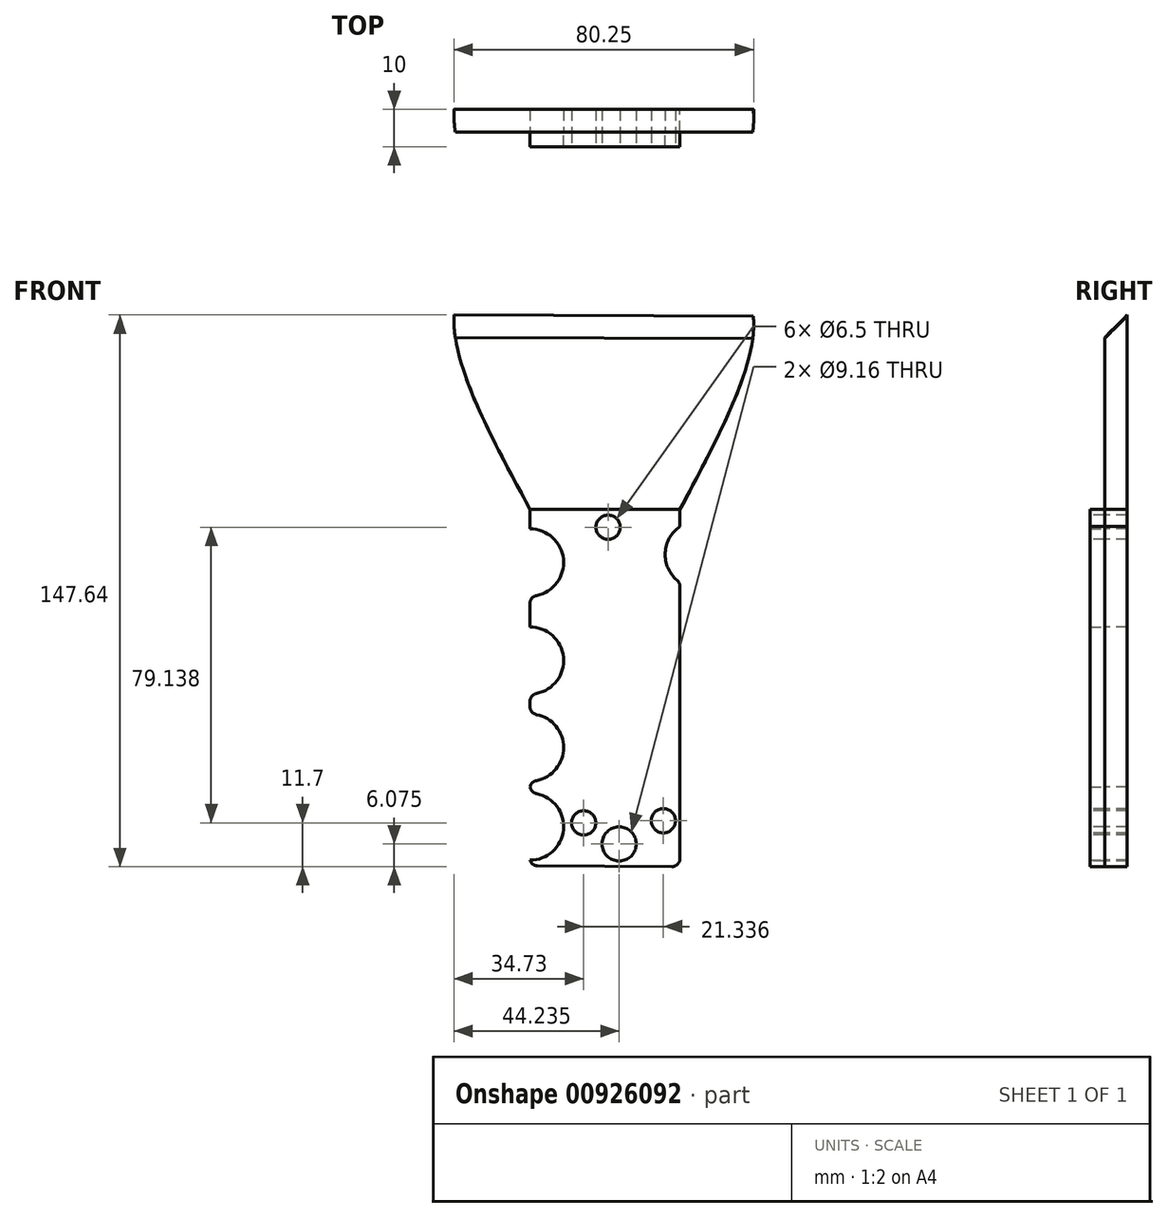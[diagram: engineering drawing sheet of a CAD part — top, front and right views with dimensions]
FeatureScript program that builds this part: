
annotation { "Feature Type Name" : "Feature", "Feature Type Description" : "" }
export const myFeature = defineFeature(function(context is Context, id is Id, definition is map)
    precondition{}
    {
        {
            var Q0;
            Q0=qCreatedBy(makeId("Front.planeOp"),FACE);
            var sketch = newSketch(context, id + "F0", { "sketchPlane" : qUnion([Q0])});
            skLineSegment(sketch, "E0.bottom", {"start": v(-40.83, 99.08) * mm, "end": v(39.17, 99.08) * mm});
            skLineSegment(sketch, "E0.top", {"start": v(-40.83, -50.92) * mm, "end": v(39.17, -50.92) * mm});
            skLineSegment(sketch, "E0.left", {"start": v(-40.83, 99.08) * mm, "end": v(-40.83, -50.92) * mm});
            skLineSegment(sketch, "E0.right", {"start": v(39.17, 99.08) * mm, "end": v(39.17, -50.92) * mm});
            skSolve(sketch);
        }
        {
            var Q0;
            Q0=makeQuery(id+"F0.imprint","IMPRINT",FACE,{"disambiguationData":[TD([[makeQuery(id+"F0.imprint","IMPRINT",EDGE,{"derivedFrom":sQuery(id+"F0.wireOp",EDGE,"E0.bottom")}),-1.0]])]});
            var sketch = newSketch(context, id + "F1", { "sketchPlane" : qUnion([Q0])});
            skLineSegment(sketch, "E1", {"start": v(-41.28, 46.44) * mm, "end": v(36.17, 46.44) * mm});
            skLineSegment(sketch, "E2", {"start": v(36.17, 46.44) * mm, "end": v(-20.92, 46.44) * mm});
            skLineSegment(sketch, "E3", {"start": v(-20.92, 46.44) * mm, "end": v(-20.92, -48.99) * mm});
            skLineSegment(sketch, "E4", {"start": v(19.24, 46.44) * mm, "end": v(19.24, -49.2) * mm});
            skLineSegment(sketch, "E5", {"start": v(-20.92, -48.99) * mm, "end": v(19.24, -49.2) * mm});
            skFitSpline(sketch, "E6", {"points": [v(-20.92, 46.44) * mm, v(-41.1, 99.43) * mm, v(-28.22, 117.54) * mm], "startDerivative": vector(-53.21, 98.2) * mm, "endDerivative": vector(46.25, 39.49) * mm});
            skFitSpline(sketch, "E7", {"points": [v(19.24, 46.44) * mm, v(38.71, 99.16) * mm, v(24.45, 116.44) * mm], "startDerivative": vector(52.8, 98.69) * mm, "endDerivative": vector(-50.13, 36.65) * mm});
            skLineSegment(sketch, "E8", {"start": v(-41.1, 99.43) * mm, "end": v(38.71, 99.16) * mm});
            skSolve(sketch);
        }
        {
            var Q0;
            Q0 = qSketchRegion(id + "F1", true);
            extrude(context, id + "F2", {"entities" : qUnion([Q0]), "depth" : 6 * mm, "offsetDistance" : 25 * mm});
        }
        {
            var Q0;
            Q0=makeQuery(id+"F2.opExtrude","CAP_EDGE",EDGE,{"disambiguationData":[OSD([sQuery(id+"F1.wireOp",EDGE,"E8")])],"isStart":false});
            chamfer(context, id + "F3", {"entities" : qUnion([Q0]), "width" : 7 * mm, "tangentPropagation" : true});
        }
        {
            var Q0;
            Q0=makeQuery(id+"F2.opExtrude","CAP_FACE",FACE,{"disambiguationData":[OSD([sQuery(id+"F1.wireOp",EDGE,"E3"),sQuery(id+"F1.wireOp",EDGE,"E4"),sQuery(id+"F1.wireOp",EDGE,"E5"),sQuery(id+"F1.wireOp",EDGE,"E6"),sQuery(id+"F1.wireOp",EDGE,"E7"),sQuery(id+"F1.wireOp",EDGE,"E8")])],"isStart":false});
            var sketch = newSketch(context, id + "F4", { "sketchPlane" : qUnion([Q0])});
            skCircle(sketch, "E9", {"center": v(-20.92, 32.19) * mm, "radius": 9 * mm});
            skCircle(sketch, "E10", {"center": v(-20.92, 5.95) * mm, "radius": 9 * mm});
            skCircle(sketch, "E11", {"center": v(-20.92, -17.34) * mm, "radius": 9 * mm});
            skCircle(sketch, "E12", {"center": v(-20.92, -38.48) * mm, "radius": 9 * mm});
            skSolve(sketch);
        }
        {
            var Q0;
            {var subQ9=sQuery(id+"F1.wireOp",EDGE,"E4");Q0=makeQuery(id+"F4.imprint","IMPRINT",FACE,{"disambiguationData":[TD([[makeQuery(id+"F4.imprint","IMPRINT",EDGE,{"derivedFrom":makeQuery(id+"F2.opExtrude","CAP_EDGE",EDGE,{"disambiguationData":[OSD([subQ9])],"isStart":false})}),-1.0]])]});}
            var sketch = newSketch(context, id + "F5", { "sketchPlane" : qUnion([Q0])});
            skCircle(sketch, "E13", {"center": v(24.28, 34.33) * mm, "radius": 9 * mm});
            skSolve(sketch);
        }
        {
            var Q0;
            {var subQ0=sQuery(id+"F4.wireOp",EDGE,"E9");var subQ1=makeQuery(id+"F2.opExtrude","CAP_EDGE",EDGE,{"disambiguationData":[OSD([sQuery(id+"F1.wireOp",EDGE,"E3")])],"isStart":false});var subQ2=makeQuery(id+"F4.imprint","INTERSECT",VERTEX,{"disambiguationData":[OD(0.0)],"derivedFrom":[subQ1,subQ0]});Q0=makeQuery(id+"F4.imprint","IMPRINT",FACE,{"disambiguationData":[TD([[makeQuery(id+"F4.imprint","IMPRINT",EDGE,{"disambiguationData":[TD([[subQ2,1.0]])],"derivedFrom":subQ0}),1.0]])]});}
            var Q1;
            {var subQ0=sQuery(id+"F4.wireOp",EDGE,"E10");var subQ1=makeQuery(id+"F2.opExtrude","CAP_EDGE",EDGE,{"disambiguationData":[OSD([sQuery(id+"F1.wireOp",EDGE,"E3")])],"isStart":false});var subQ2=makeQuery(id+"F4.imprint","INTERSECT",VERTEX,{"disambiguationData":[OD(0.0)],"derivedFrom":[subQ1,subQ0]});Q1=makeQuery(id+"F4.imprint","IMPRINT",FACE,{"disambiguationData":[TD([[makeQuery(id+"F4.imprint","IMPRINT",EDGE,{"disambiguationData":[TD([[subQ2,1.0]])],"derivedFrom":subQ0}),1.0]])]});}
            var Q2;
            {var subQ0=sQuery(id+"F4.wireOp",EDGE,"E11");var subQ1=makeQuery(id+"F2.opExtrude","CAP_EDGE",EDGE,{"disambiguationData":[OSD([sQuery(id+"F1.wireOp",EDGE,"E3")])],"isStart":false});var subQ2=makeQuery(id+"F4.imprint","INTERSECT",VERTEX,{"disambiguationData":[OD(0.0)],"derivedFrom":[subQ1,subQ0]});Q2=makeQuery(id+"F4.imprint","IMPRINT",FACE,{"disambiguationData":[TD([[makeQuery(id+"F4.imprint","IMPRINT",EDGE,{"disambiguationData":[TD([[subQ2,-1.0]])],"derivedFrom":subQ0}),1.0]])]});}
            var Q3;
            {var subQ0=sQuery(id+"F4.wireOp",EDGE,"E12");var subQ1=makeQuery(id+"F2.opExtrude","CAP_EDGE",EDGE,{"disambiguationData":[OSD([sQuery(id+"F1.wireOp",EDGE,"E3")])],"isStart":false});var subQ2=makeQuery(id+"F4.imprint","INTERSECT",VERTEX,{"disambiguationData":[OD(0.0)],"derivedFrom":[subQ1,subQ0]});Q3=makeQuery(id+"F4.imprint","IMPRINT",FACE,{"disambiguationData":[TD([[makeQuery(id+"F4.imprint","IMPRINT",EDGE,{"disambiguationData":[TD([[subQ2,-1.0]])],"derivedFrom":subQ0}),1.0]])]});}
            var Q4;
            {var subQ0=sQuery(id+"F5.wireOp",EDGE,"E13");var subQ1=makeQuery(id+"F4.imprint","IMPRINT",EDGE,{"derivedFrom":makeQuery(id+"F2.opExtrude","CAP_EDGE",EDGE,{"disambiguationData":[OSD([sQuery(id+"F1.wireOp",EDGE,"E4")])],"isStart":false})});var subQ2=makeQuery(id+"F5.imprint","INTERSECT",VERTEX,{"disambiguationData":[OD(0.0)],"derivedFrom":[subQ1,subQ0]});Q4=makeQuery(id+"F5.imprint","IMPRINT",FACE,{"disambiguationData":[TD([[makeQuery(id+"F5.imprint","IMPRINT",EDGE,{"disambiguationData":[TD([[subQ2,-1.0]])],"derivedFrom":subQ0}),1.0]])]});}
            extrude(context, id + "F6", {"entities" : qUnion([Q0, Q1, Q2, Q3, Q4]), "operationType" : NewBodyOperationType.REMOVE, "oppositeDirection" : true, "depth" : 25 * mm, "offsetDistance" : 25 * mm});
        }
        {
            var Q0;
            {var subQ0=sQuery(id+"F4.wireOp",EDGE,"E9");var subQ1=sQuery(id+"F1.wireOp",EDGE,"E3");Q0=makeQuery(id+"F6.boolean.opBoolean","COPY",EDGE,{"derivedFrom":makeQuery(id+"F6.opExtrude","SWEPT_EDGE",EDGE,{"disambiguationData":[OSD([subQ1,subQ0]),TDD([makeQuery(id+"F4.imprint","INTERSECT",VERTEX,{"disambiguationData":[OD(1.0)],"derivedFrom":[makeQuery(id+"F2.opExtrude","CAP_EDGE",EDGE,{"disambiguationData":[OSD([subQ1])],"isStart":false}),subQ0]})])]})});}
            var Q1;
            {var subQ0=sQuery(id+"F4.wireOp",EDGE,"E10");var subQ1=sQuery(id+"F1.wireOp",EDGE,"E3");Q1=makeQuery(id+"F6.boolean.opBoolean","COPY",EDGE,{"derivedFrom":makeQuery(id+"F6.opExtrude","SWEPT_EDGE",EDGE,{"disambiguationData":[OSD([subQ1,subQ0]),TDD([makeQuery(id+"F4.imprint","INTERSECT",VERTEX,{"disambiguationData":[OD(1.0)],"derivedFrom":[makeQuery(id+"F2.opExtrude","CAP_EDGE",EDGE,{"disambiguationData":[OSD([subQ1])],"isStart":false}),subQ0]})])]})});}
            var Q2;
            {var subQ0=sQuery(id+"F4.wireOp",EDGE,"E11");var subQ1=sQuery(id+"F1.wireOp",EDGE,"E3");Q2=makeQuery(id+"F6.boolean.opBoolean","COPY",EDGE,{"derivedFrom":makeQuery(id+"F6.opExtrude","SWEPT_EDGE",EDGE,{"disambiguationData":[OSD([subQ1,subQ0]),TDD([makeQuery(id+"F4.imprint","INTERSECT",VERTEX,{"disambiguationData":[OD(1.0)],"derivedFrom":[makeQuery(id+"F2.opExtrude","CAP_EDGE",EDGE,{"disambiguationData":[OSD([subQ1])],"isStart":false}),subQ0]})])]})});}
            var Q3;
            {var subQ0=sQuery(id+"F4.wireOp",EDGE,"E11");var subQ1=sQuery(id+"F1.wireOp",EDGE,"E3");Q3=makeQuery(id+"F6.boolean.opBoolean","COPY",EDGE,{"derivedFrom":makeQuery(id+"F6.opExtrude","SWEPT_EDGE",EDGE,{"disambiguationData":[OSD([subQ1,subQ0]),TDD([makeQuery(id+"F4.imprint","INTERSECT",VERTEX,{"disambiguationData":[OD(0.0)],"derivedFrom":[makeQuery(id+"F2.opExtrude","CAP_EDGE",EDGE,{"disambiguationData":[OSD([subQ1])],"isStart":false}),subQ0]})])]})});}
            var Q4;
            {var subQ0=sQuery(id+"F4.wireOp",EDGE,"E12");var subQ1=sQuery(id+"F1.wireOp",EDGE,"E3");Q4=makeQuery(id+"F6.boolean.opBoolean","COPY",EDGE,{"derivedFrom":makeQuery(id+"F6.opExtrude","SWEPT_EDGE",EDGE,{"disambiguationData":[OSD([subQ1,subQ0]),TDD([makeQuery(id+"F4.imprint","INTERSECT",VERTEX,{"disambiguationData":[OD(1.0)],"derivedFrom":[makeQuery(id+"F2.opExtrude","CAP_EDGE",EDGE,{"disambiguationData":[OSD([subQ1])],"isStart":false}),subQ0]})])]})});}
            var Q5;
            Q5=makeQuery(id+"F2.opExtrude","SWEPT_EDGE",EDGE,{"disambiguationData":[OSD([sQuery(id+"F1.wireOp",EDGE,"E3"),sQuery(id+"F1.wireOp",EDGE,"E5")])]});
            var Q6;
            Q6=makeQuery(id+"F2.opExtrude","SWEPT_EDGE",EDGE,{"disambiguationData":[OSD([sQuery(id+"F1.wireOp",EDGE,"E4"),sQuery(id+"F1.wireOp",EDGE,"E5")])]});
            var Q7;
            {var subQ0=sQuery(id+"F5.wireOp",EDGE,"E13");var subQ1=sQuery(id+"F1.wireOp",EDGE,"E4");Q7=makeQuery(id+"F6.boolean.opBoolean","COPY",EDGE,{"derivedFrom":makeQuery(id+"F6.opExtrude","SWEPT_EDGE",EDGE,{"disambiguationData":[OSD([subQ1,subQ0]),TDD([makeQuery(id+"F5.imprint","INTERSECT",VERTEX,{"disambiguationData":[OD(0.0)],"derivedFrom":[makeQuery(id+"F4.imprint","IMPRINT",EDGE,{"derivedFrom":makeQuery(id+"F2.opExtrude","CAP_EDGE",EDGE,{"disambiguationData":[OSD([subQ1])],"isStart":false})}),subQ0]})])]})});}
            var Q8;
            {var subQ0=sQuery(id+"F5.wireOp",EDGE,"E13");var subQ1=sQuery(id+"F1.wireOp",EDGE,"E4");Q8=makeQuery(id+"F6.boolean.opBoolean","COPY",EDGE,{"derivedFrom":makeQuery(id+"F6.opExtrude","SWEPT_EDGE",EDGE,{"disambiguationData":[OSD([subQ1,subQ0]),TDD([makeQuery(id+"F5.imprint","INTERSECT",VERTEX,{"disambiguationData":[OD(1.0)],"derivedFrom":[makeQuery(id+"F4.imprint","IMPRINT",EDGE,{"derivedFrom":makeQuery(id+"F2.opExtrude","CAP_EDGE",EDGE,{"disambiguationData":[OSD([subQ1])],"isStart":false})}),subQ0]})])]})});}
            fillet(context, id + "F7", {"entities" : qUnion([Q0, Q1, Q2, Q3, Q4, Q5, Q6, Q7, Q8]), "radius" : 2.17 * mm, "tangentPropagation" : true, "allowEdgeOverflow" : false});
        }
        {
            var Q0;
            Q0=makeQuery(id+"F2.opExtrude","CAP_FACE",FACE,{"disambiguationData":[OSD([sQuery(id+"F1.wireOp",EDGE,"E3"),sQuery(id+"F1.wireOp",EDGE,"E4"),sQuery(id+"F1.wireOp",EDGE,"E5"),sQuery(id+"F1.wireOp",EDGE,"E6"),sQuery(id+"F1.wireOp",EDGE,"E7"),sQuery(id+"F1.wireOp",EDGE,"E8")])],"isStart":false});
            var sketch = newSketch(context, id + "F8", { "sketchPlane" : qUnion([Q0])});
            skLineSegment(sketch, "E14", {"start": v(-20.92, 46.44) * mm, "end": v(19.24, 46.44) * mm});
            skSolve(sketch);
        }
        {
            var Q0;
            Q0=makeQuery(id+"F8.imprint","IMPRINT",FACE,{"disambiguationData":[TD([[makeQuery(id+"F8.imprint","IMPRINT",EDGE,{"derivedFrom":sQuery(id+"F8.wireOp",EDGE,"E14")}),-1.0]])]});
            extrude(context, id + "F9", {"entities" : qUnion([Q0]), "depth" : 4 * mm, "offsetDistance" : 25 * mm});
        }
        {
            var Q0;
            Q0=makeQuery(id+"F9.opExtrude","CAP_FACE",FACE,{"disambiguationData":[OSD([sQuery(id+"F1.wireOp",EDGE,"E3"),sQuery(id+"F1.wireOp",EDGE,"E4"),sQuery(id+"F1.wireOp",EDGE,"E5"),sQuery(id+"F1.wireOp",EDGE,"E6"),sQuery(id+"F1.wireOp",EDGE,"E7"),sQuery(id+"F1.wireOp",EDGE,"E8"),sQuery(id+"F4.wireOp",EDGE,"E9"),sQuery(id+"F4.wireOp",EDGE,"E10"),sQuery(id+"F4.wireOp",EDGE,"E11"),sQuery(id+"F4.wireOp",EDGE,"E12"),sQuery(id+"F5.wireOp",EDGE,"E13"),sQuery(id+"F8.wireOp",EDGE,"E14")])],"isStart":false});
            var sketch = newSketch(context, id + "F10", { "sketchPlane" : qUnion([Q0])});
            skCircle(sketch, "E15", {"center": v(-6.54, -37.5) * mm, "radius": 3.25 * mm});
            skCircle(sketch, "E16", {"center": v(0, 41.64) * mm, "radius": 3.25 * mm});
            skCircle(sketch, "E17", {"center": v(14.8, -36.92) * mm, "radius": 3.25 * mm});
            skCircle(sketch, "E18", {"center": v(2.96, -43.12) * mm, "radius": 4.58 * mm});
            skSolve(sketch);
        }
        {
            var Q0;
            Q0=makeQuery(id+"F10.imprint","IMPRINT",FACE,{"disambiguationData":[TD([[makeQuery(id+"F10.imprint","IMPRINT",EDGE,{"derivedFrom":sQuery(id+"F10.wireOp",EDGE,"E16")}),1.0]])]});
            var Q1;
            Q1=makeQuery(id+"F10.imprint","IMPRINT",FACE,{"disambiguationData":[TD([[makeQuery(id+"F10.imprint","IMPRINT",EDGE,{"derivedFrom":sQuery(id+"F10.wireOp",EDGE,"E15")}),1.0]])]});
            var Q2;
            Q2=makeQuery(id+"F10.imprint","IMPRINT",FACE,{"disambiguationData":[TD([[makeQuery(id+"F10.imprint","IMPRINT",EDGE,{"derivedFrom":sQuery(id+"F10.wireOp",EDGE,"E18")}),1.0]])]});
            var Q3;
            Q3=makeQuery(id+"F10.imprint","IMPRINT",FACE,{"disambiguationData":[TD([[makeQuery(id+"F10.imprint","IMPRINT",EDGE,{"derivedFrom":sQuery(id+"F10.wireOp",EDGE,"E17")}),1.0]])]});
            extrude(context, id + "F11", {"entities" : qUnion([Q0, Q1, Q2, Q3]), "operationType" : NewBodyOperationType.REMOVE, "oppositeDirection" : true, "depth" : 25 * mm, "offsetDistance" : 25 * mm});
        }
    });
